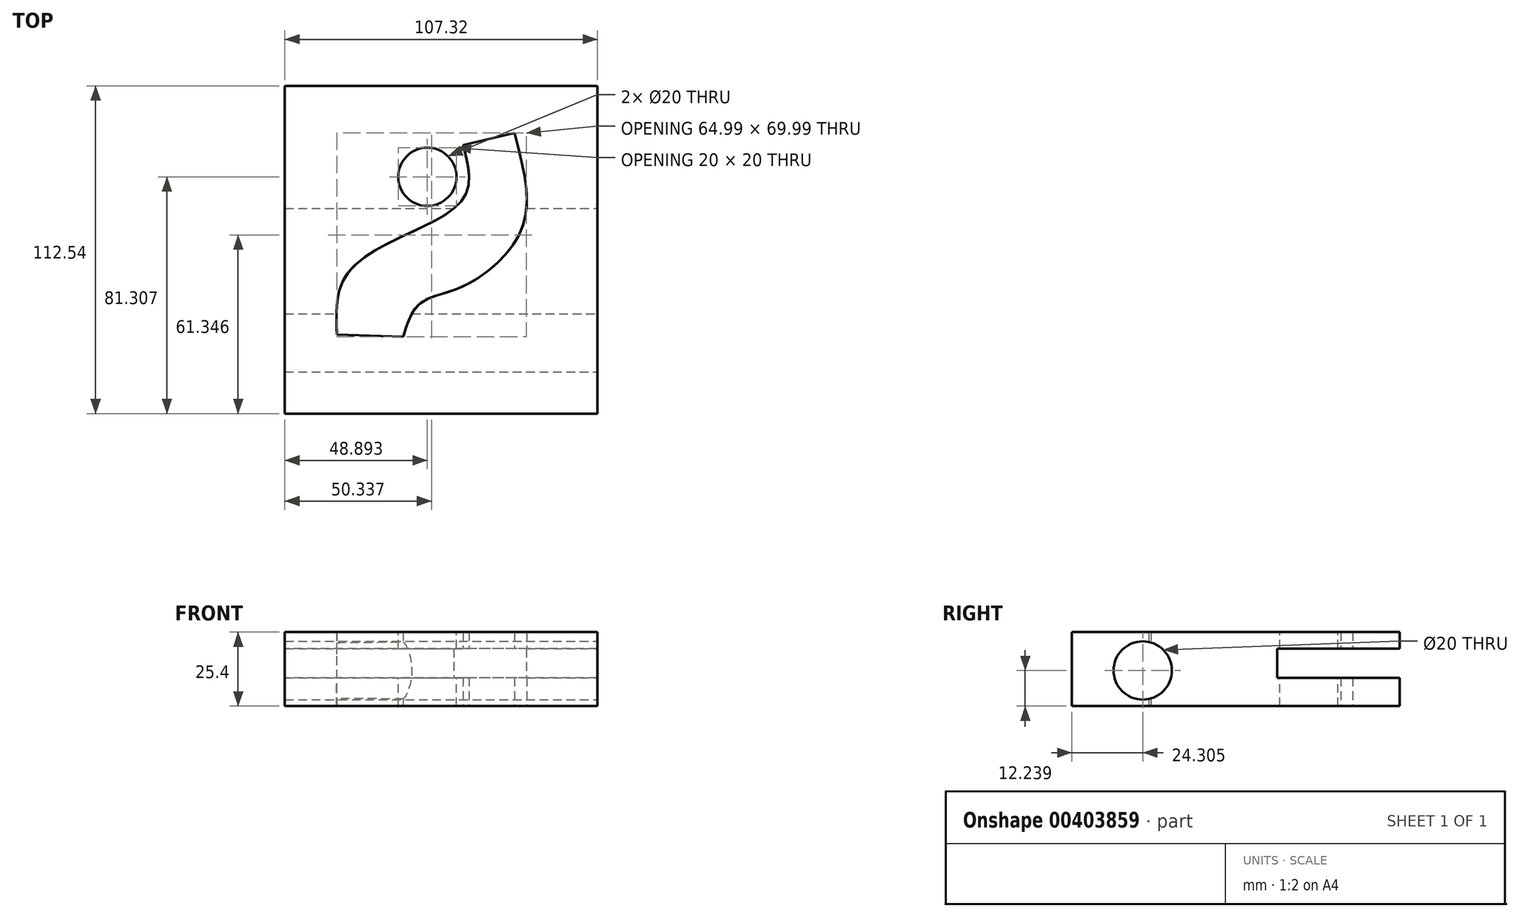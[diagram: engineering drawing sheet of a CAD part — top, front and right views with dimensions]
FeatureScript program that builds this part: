
annotation { "Feature Type Name" : "Feature", "Feature Type Description" : "" }
export const myFeature = defineFeature(function(context is Context, id is Id, definition is map)
    precondition{}
    {
        {
            var Q0;
            Q0=qCreatedBy(makeId("Top.planeOp"),FACE);
            var sketch = newSketch(context, id + "F0", { "sketchPlane" : qUnion([Q0])});
            skLineSegment(sketch, "E0.bottom", {"start": v(-54.62, 55.86) * mm, "end": v(52.7, 55.86) * mm});
            skLineSegment(sketch, "E0.top", {"start": v(-54.62, -56.68) * mm, "end": v(52.7, -56.68) * mm});
            skLineSegment(sketch, "E0.left", {"start": v(-54.62, 55.86) * mm, "end": v(-54.62, -56.68) * mm});
            skLineSegment(sketch, "E0.right", {"start": v(52.7, 55.86) * mm, "end": v(52.7, -56.68) * mm});
            skFitSpline(sketch, "E1", {"points": [v(-36.78, -29.5) * mm, v(-33.76, -9.47) * mm, v(-11.25, 5.63) * mm, v(7.41, 18.53) * mm, v(6.59, 35.54) * mm], "startDerivative": vector(-3.64, 89.27) * mm, "endDerivative": vector(-21.15, 82.97) * mm});
            skFitSpline(sketch, "E2", {"points": [v(-14, -30.33) * mm, v(-8.5, -19.08) * mm, v(4.4, -13.86) * mm, v(20.31, -2.88) * mm, v(28.27, 13.31) * mm, v(24.15, 39.66) * mm], "startDerivative": vector(22.89, 77.92) * mm, "endDerivative": vector(-30.54, 114.07) * mm});
            skLineSegment(sketch, "E3", {"start": v(6.59, 35.54) * mm, "end": v(24.15, 39.66) * mm});
            skLineSegment(sketch, "E4", {"start": v(-36.78, -29.5) * mm, "end": v(-14, -30.33) * mm});
            skSolve(sketch);
        }
        {
            var Q0;
            Q0 = qSketchRegion(id + "F0", true);
            extrude(context, id + "F1", {"entities" : qUnion([Q0]), "depth" : 25.4 * mm});
        }
        {
            var Q0;
            Q0=makeQuery(id+"F1.opExtrude","SWEPT_FACE",FACE,{"disambiguationData":[OSD([sQuery(id+"F0.wireOp",EDGE,"E0.right")])]});
            var sketch = newSketch(context, id + "F2", { "sketchPlane" : qUnion([Q0])});
            skCircle(sketch, "E5", {"center": v(-32.38, 12.24) * mm, "radius": 10 * mm});
            skLineSegment(sketch, "E6.bottom", {"start": v(13.77, 19.73) * mm, "end": v(57.9, 19.73) * mm});
            skLineSegment(sketch, "E6.top", {"start": v(13.77, 9.73) * mm, "end": v(57.9, 9.73) * mm});
            skLineSegment(sketch, "E6.left", {"start": v(13.77, 19.73) * mm, "end": v(13.77, 9.73) * mm});
            skLineSegment(sketch, "E6.right", {"start": v(57.9, 19.73) * mm, "end": v(57.9, 9.73) * mm});
            skSolve(sketch);
        }
        {
            var Q0;
            Q0 = qSketchRegion(id + "F2", true);
            extrude(context, id + "F3", {"entities" : qUnion([Q0]), "operationType" : NewBodyOperationType.REMOVE, "endBound" : BoundingType.THROUGH_ALL, "oppositeDirection" : true, "depth" : 25 * mm});
        }
        {
            var Q0;
            Q0=makeQuery(id+"F1.opExtrude","CAP_FACE",FACE,{"disambiguationData":[OSD([sQuery(id+"F0.wireOp",EDGE,"E0.bottom"),sQuery(id+"F0.wireOp",EDGE,"E0.top"),sQuery(id+"F0.wireOp",EDGE,"E0.left"),sQuery(id+"F0.wireOp",EDGE,"E0.right"),sQuery(id+"F0.wireOp",EDGE,"E1"),sQuery(id+"F0.wireOp",EDGE,"E2"),sQuery(id+"F0.wireOp",EDGE,"E3"),sQuery(id+"F0.wireOp",EDGE,"E4")])],"isStart":false});
            var sketch = newSketch(context, id + "F4", { "sketchPlane" : qUnion([Q0])});
            skCircle(sketch, "E7", {"center": v(-5.73, 24.63) * mm, "radius": 10 * mm});
            skSolve(sketch);
        }
        {
            var Q0;
            Q0 = qSketchRegion(id + "F4", true);
            extrude(context, id + "F5", {"entities" : qUnion([Q0]), "operationType" : NewBodyOperationType.REMOVE, "endBound" : BoundingType.THROUGH_ALL, "oppositeDirection" : true, "depth" : 25 * mm});
        }
    });
